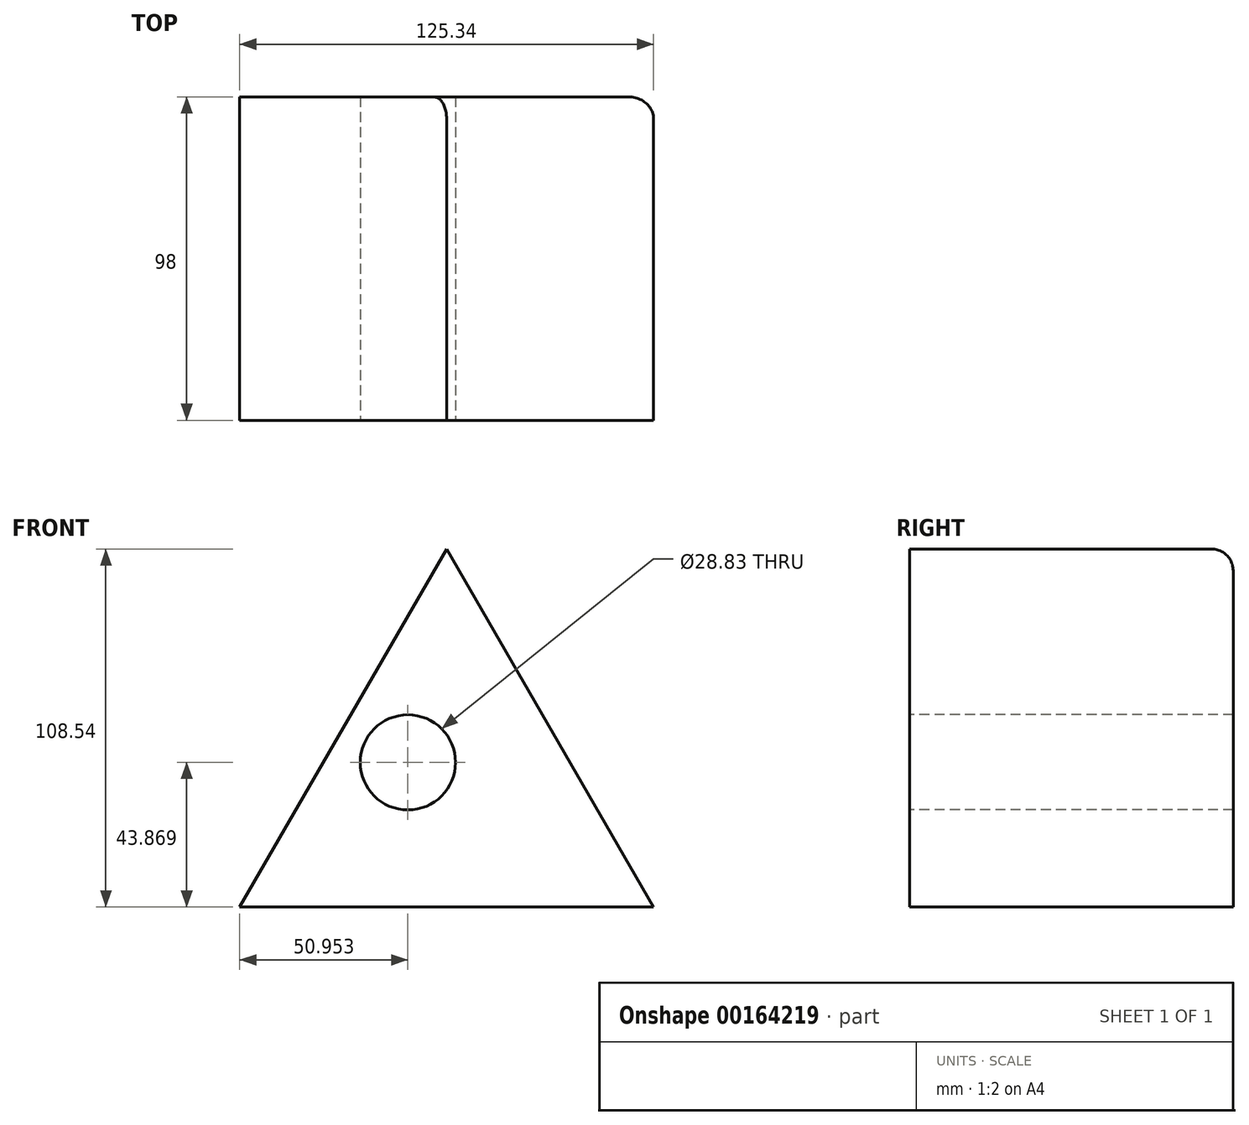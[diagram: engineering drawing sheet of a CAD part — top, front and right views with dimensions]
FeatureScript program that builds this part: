
annotation { "Feature Type Name" : "Feature", "Feature Type Description" : "" }
export const myFeature = defineFeature(function(context is Context, id is Id, definition is map)
    precondition{}
    {
        {
            var Q0;
            Q0=qCreatedBy(makeId("Front.planeOp"),FACE);
            var sketch = newSketch(context, id + "F0", { "sketchPlane" : qUnion([Q0])});
            skCircle(sketch, "E0.cCircle", {"center": v(0, 0) * mm, "radius": 36.18 * mm, "construction": true});
            skLineSegment(sketch, "E0.0", {"start": v(62.67, -36.18) * mm, "end": v(-62.67, -36.18) * mm});
            skLineSegment(sketch, "E0.1", {"start": v(-62.67, -36.18) * mm, "end": v(0, 72.36) * mm});
            skLineSegment(sketch, "E0.2", {"start": v(0, 72.36) * mm, "end": v(62.67, -36.18) * mm});
            skPoint(sketch, "E0.0.midPoint", {"position": v(0, -36.18) * mm});
            skSolve(sketch);
        }
        {
            var Q0;
            Q0=makeQuery(id+"F0.imprint","IMPRINT",FACE,{"disambiguationData":[TD([[makeQuery(id+"F0.imprint","IMPRINT",EDGE,{"derivedFrom":sQuery(id+"F0.wireOp",EDGE,"E0.0")}),-1.0]])]});
            extrude(context, id + "F1", {"entities" : qUnion([Q0]), "depth" : 98 * mm});
        }
        {
            var Q0;
            Q0=makeQuery(id+"F1.opExtrude","CAP_EDGE",EDGE,{"disambiguationData":[OSD([sQuery(id+"F0.wireOp",EDGE,"E0.2")])],"isStart":true});
            fillet(context, id + "F2", {"entities" : qUnion([Q0]), "radius" : 6.52 * mm, "tangentPropagation" : true, "allowEdgeOverflow" : false});
        }
        {
            var Q0;
            Q0=makeQuery(id+"F1.opExtrude","CAP_FACE",FACE,{"disambiguationData":[OSD([sQuery(id+"F0.wireOp",EDGE,"E0.0"),sQuery(id+"F0.wireOp",EDGE,"E0.1"),sQuery(id+"F0.wireOp",EDGE,"E0.2")])],"isStart":false});
            var sketch = newSketch(context, id + "F3", { "sketchPlane" : qUnion([Q0])});
            skCircle(sketch, "E1", {"center": v(-11.72, 7.69) * mm, "radius": 14.42 * mm});
            skSolve(sketch);
        }
        {
            var Q0;
            Q0=makeQuery(id+"F3.imprint","IMPRINT",FACE,{"disambiguationData":[TD([[makeQuery(id+"F3.imprint","IMPRINT",EDGE,{"derivedFrom":sQuery(id+"F3.wireOp",EDGE,"E1")}),1.0]])]});
            extrude(context, id + "F4", {"entities" : qUnion([Q0]), "operationType" : NewBodyOperationType.REMOVE, "endBound" : BoundingType.THROUGH_ALL, "oppositeDirection" : true, "depth" : 25 * mm});
        }
    });
